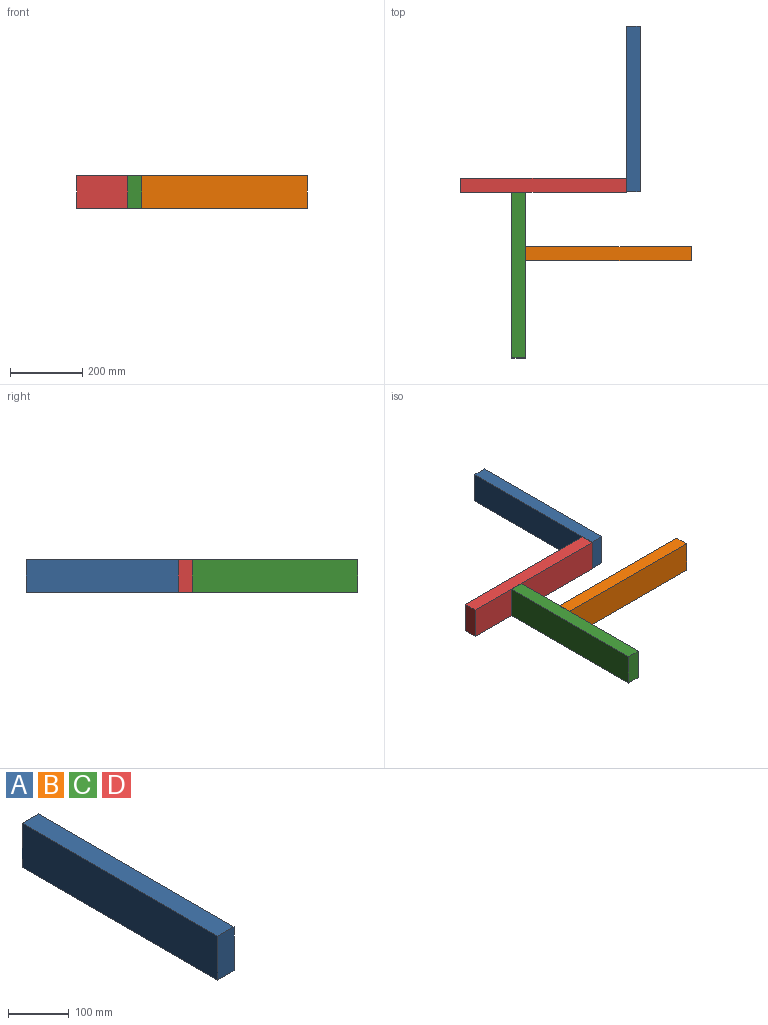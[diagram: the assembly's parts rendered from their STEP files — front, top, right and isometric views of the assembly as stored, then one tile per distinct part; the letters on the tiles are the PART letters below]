
ASSEMBLY  parts=4 mates=6
PART A: 6 faces, bbox 38.1x457.2x88.9 mm
  f0: plane 457.2x88.9mm, normal (-1,0,0), area 40645.1mm2, adj f1,f3,f4,f5
  f1: plane 457.2x38.1mm, normal (0,0,-1), area 17419.3mm2, adj f0,f2,f4,f5
  f2: plane 457.2x88.9mm, normal (1,0,0), area 40645.1mm2, adj f1,f3,f4,f5
  f3: plane 457.2x38.1mm, normal (0,0,1), area 17419.3mm2, adj f0,f2,f4,f5
  f4: plane 88.9x38.1mm, normal (0,-1,0), area 3387.1mm2, adj f0,f1,f2,f3
  f5: plane 88.9x38.1mm, normal (0,1,0), area 3387.1mm2, adj f0,f1,f2,f3
PART B: same geometry as A
PART C: same geometry as A
PART D: same geometry as A
PLACE A rot(axis=(1,0,0),180deg) t=(-105.61,-319.4,86.19)mm
PLACE B rot(axis=(0,0,-1),90deg) t=(73.47,-471.45,-2.71)mm
PLACE C t=(-421.83,-320.89,-2.71)mm
PLACE D rot(axis=(0.71,0.71,0),180deg) t=(-105.61,-320.89,86.19)mm
MATE planar D.f0 <-> C.f5  axis (0,-1,0) through (-334.21,-320.89,41.74)mm
MATE planar A.f1 <-> D.f1  axis (0,0,1) through (-105.61,-90.8,86.19)mm
MATE planar B.f4 <-> C.f2  axis (-1,0,0) through (-383.73,-490.5,41.74)mm
MATE planar A.f0 <-> D.f5  axis (-1,0,0) through (-105.61,-90.8,41.74)mm
MATE planar C.f3 <-> D.f1  axis (0,0,1) through (-402.78,-549.49,86.19)mm
MATE planar B.f3 <-> A.f1  axis (0,0,1) through (-155.13,-490.5,86.19)mm
